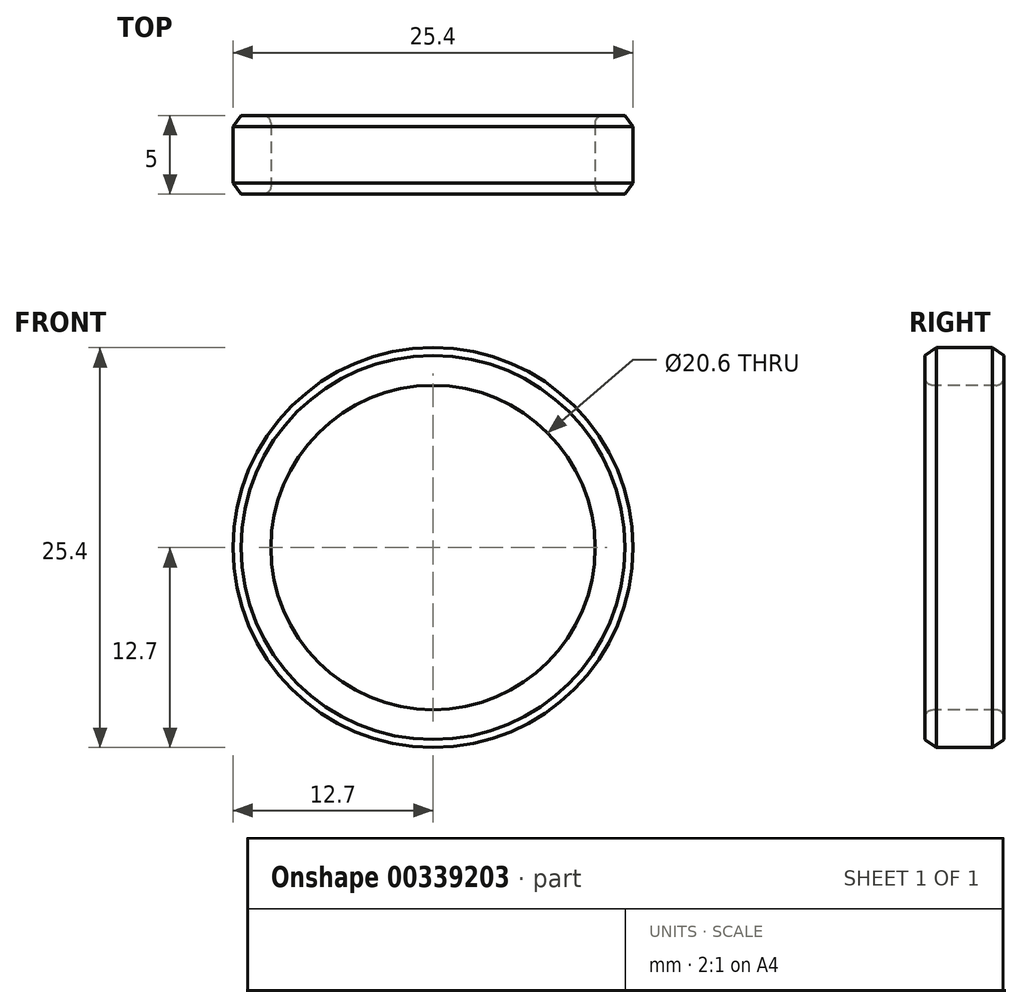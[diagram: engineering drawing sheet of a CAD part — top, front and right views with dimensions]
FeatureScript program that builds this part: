
annotation { "Feature Type Name" : "Feature", "Feature Type Description" : "" }
export const myFeature = defineFeature(function(context is Context, id is Id, definition is map)
    precondition{}
    {
        {
            var Q0;
            Q0=qCreatedBy(makeId("Right.planeOp"),FACE);
            var sketch = newSketch(context, id + "F0", { "sketchPlane" : qUnion([Q0])});
            skLineSegment(sketch, "E0", {"start": v(0, 0) * mm, "end": v(16.48, 0) * mm, "construction": true});
            skLineSegment(sketch, "E1", {"start": v(0, 0) * mm, "end": v(0, 10.3) * mm, "construction": true});
            skLineSegment(sketch, "E2.top", {"start": v(-2, 10.3) * mm, "end": v(0, 10.3) * mm});
            skLineSegment(sketch, "E2.right", {"start": v(2.5, 12.7) * mm, "end": v(2.5, 10.3) * mm, "construction": true});
            skLineSegment(sketch, "E3", {"start": v(0, 10.3) * mm, "end": v(0, 12.7) * mm});
            skLineSegment(sketch, "E4", {"start": v(0, 12.7) * mm, "end": v(2.5, 12.7) * mm, "construction": true});
            skLineSegment(sketch, "E5", {"start": v(0, 10.3) * mm, "end": v(2.5, 10.3) * mm, "construction": true});
            skLineSegment(sketch, "E6", {"start": v(-2.5, 12.2) * mm, "end": v(-2.5, 10.8) * mm});
            skLineSegment(sketch, "E7", {"start": v(-2.5, 12.2) * mm, "end": v(-1.79, 12.7) * mm});
            skLineSegment(sketch, "E8", {"start": v(-1.79, 12.7) * mm, "end": v(0, 12.7) * mm});
            skPoint(sketch, "E9.visualSharp", {"position": v(-2.5, 10.3) * mm});
            skArc(sketch, "E9.filletArc", {"start": v(-2.5, 10.8) * mm, "mid": v(-2.35, 10.45) * mm, "end": v(-2, 10.3) * mm});
            skSolve(sketch);
        }
        {
            var Q0;
            Q0 = qSketchRegion(id + "F0", true);
            var Q1;
            Q1=sQuery(id+"F0.wireOp",EDGE,"E0");
            revolve(context, id + "F1", {"entities" : qUnion([Q0]), "axis" : qUnion([Q1]), "revolveType" : RevolveType.FULL});
        }
        {
            var Q0;
            Q0=makeQuery(id+"F1.opRevolve","SWEPT_BODY",BODY,{"disambiguationData":[OSD([sQuery(id+"F0.wireOp",EDGE,"E2.top"),sQuery(id+"F0.wireOp",EDGE,"E3"),sQuery(id+"F0.wireOp",EDGE,"E6"),sQuery(id+"F0.wireOp",EDGE,"E7"),sQuery(id+"F0.wireOp",EDGE,"E8"),sQuery(id+"F0.wireOp",EDGE,"E9.filletArc")])]});
            var Q1;
            Q1=qCreatedBy(makeId("Front.planeOp"),FACE);
            mirror(context, id + "F2", {"operationType" : NewBodyOperationType.ADD, "entities" : qUnion([Q0]), "mirrorPlane" : qUnion([Q1])});
        }
    });
